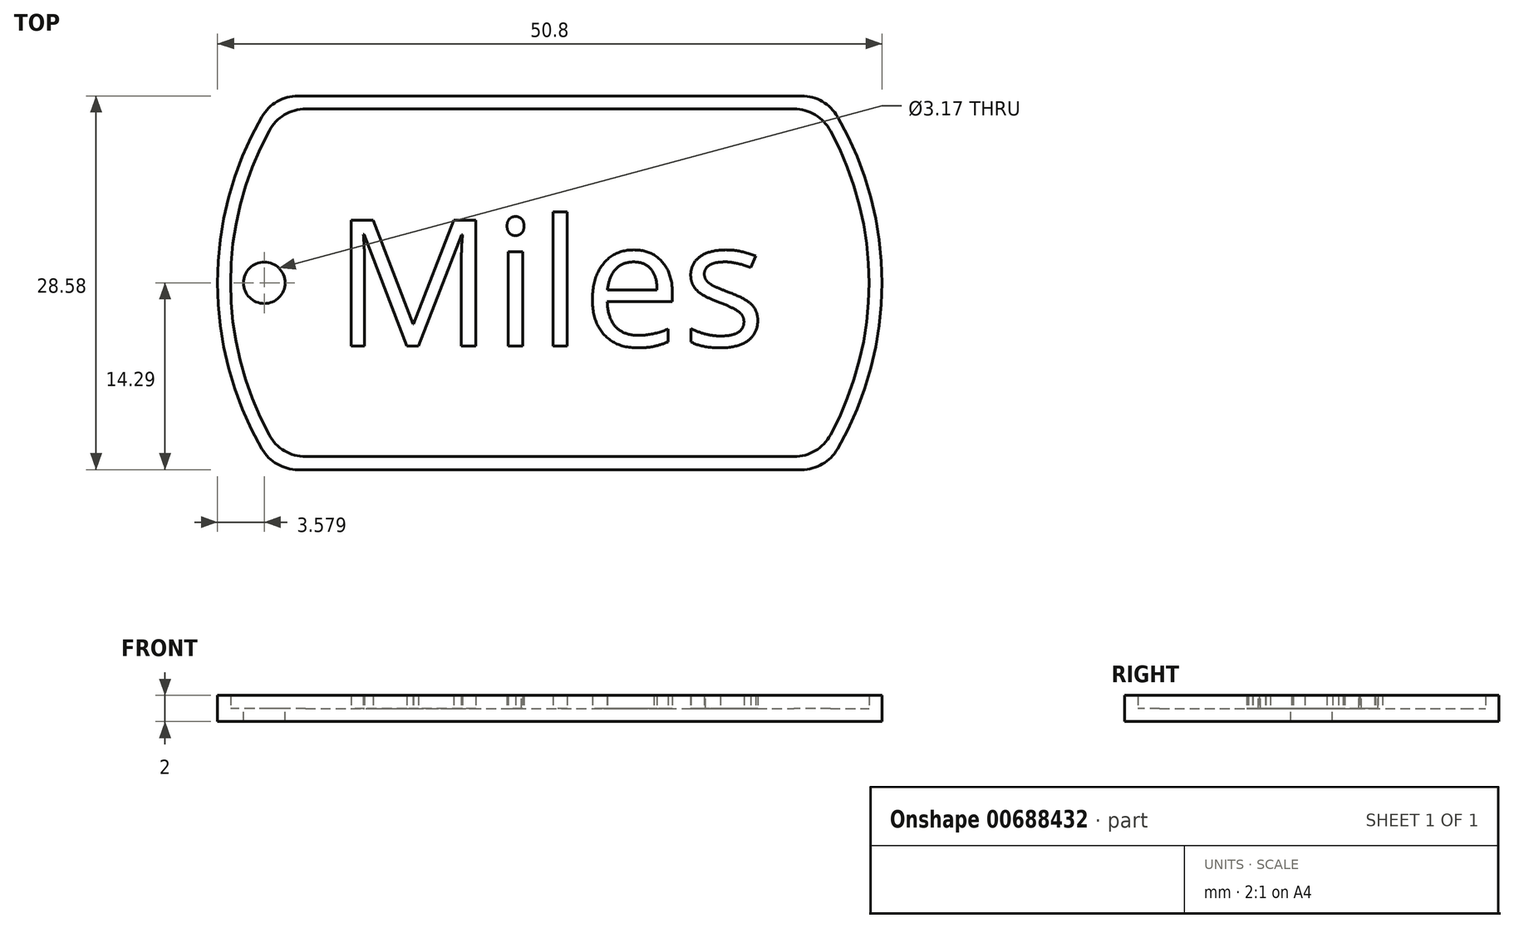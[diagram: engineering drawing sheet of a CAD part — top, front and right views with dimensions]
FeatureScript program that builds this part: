
annotation { "Feature Type Name" : "Feature", "Feature Type Description" : "" }
export const myFeature = defineFeature(function(context is Context, id is Id, definition is map)
    precondition{}
    {
        {
            var Q0;
            Q0=qCreatedBy(makeId("Top.planeOp"),FACE);
            var sketch = newSketch(context, id + "F0", { "sketchPlane" : qUnion([Q0])});
            skArc(sketch, "E0", {"start": v(-22, 12.7) * mm, "mid": v(-25.4, 0) * mm, "end": v(-22, -12.7) * mm});
            skLineSegment(sketch, "E1.top", {"start": v(-19.25, -14.29) * mm, "end": v(19.25, -14.29) * mm});
            skArc(sketch, "E2.trimOffspring", {"start": v(22, -12.7) * mm, "mid": v(25.4, 0) * mm, "end": v(22, 12.7) * mm});
            skLineSegment(sketch, "E3", {"start": v(-19.25, 14.29) * mm, "end": v(19.25, 14.29) * mm});
            skPoint(sketch, "E4.visualSharp", {"position": v(-21, 14.29) * mm});
            skArc(sketch, "E4.filletArc", {"start": v(-19.25, 14.29) * mm, "mid": v(-20.83, 13.86) * mm, "end": v(-22, 12.7) * mm});
            skPoint(sketch, "E5.visualSharp", {"position": v(21, 14.29) * mm});
            skArc(sketch, "E5.filletArc", {"start": v(22, 12.7) * mm, "mid": v(20.83, 13.86) * mm, "end": v(19.25, 14.29) * mm});
            skPoint(sketch, "E6.visualSharp", {"position": v(21, -14.29) * mm});
            skArc(sketch, "E6.filletArc", {"start": v(19.25, -14.29) * mm, "mid": v(20.83, -13.86) * mm, "end": v(22, -12.7) * mm});
            skPoint(sketch, "E7.visualSharp", {"position": v(-21, -14.29) * mm});
            skArc(sketch, "E7.filletArc", {"start": v(-22, -12.7) * mm, "mid": v(-20.83, -13.86) * mm, "end": v(-19.25, -14.29) * mm});
            skSolve(sketch);
        }
        {
            var Q0;
            Q0=makeQuery(id+"F0.imprint","IMPRINT",FACE,{"disambiguationData":[TD([[makeQuery(id+"F0.imprint","IMPRINT",EDGE,{"derivedFrom":sQuery(id+"F0.wireOp",EDGE,"E0")}),1.0]])]});
            extrude(context, id + "F1", {"entities" : qUnion([Q0]), "depth" : 1 * mm, "offsetDistance" : 25.4 * mm});
        }
        {
            var Q0;
            Q0=makeQuery(id+"F1.opExtrude","CAP_FACE",FACE,{"disambiguationData":[OSD([sQuery(id+"F0.wireOp",EDGE,"E0"),sQuery(id+"F0.wireOp",EDGE,"E1.top"),sQuery(id+"F0.wireOp",EDGE,"E2.trimOffspring"),sQuery(id+"F0.wireOp",EDGE,"E3"),sQuery(id+"F0.wireOp",EDGE,"E4.filletArc"),sQuery(id+"F0.wireOp",EDGE,"E5.filletArc"),sQuery(id+"F0.wireOp",EDGE,"E6.filletArc"),sQuery(id+"F0.wireOp",EDGE,"E7.filletArc")])],"isStart":false});
            var sketch = newSketch(context, id + "F2", { "sketchPlane" : qUnion([Q0])});
            skLineSegment(sketch, "E8.0", {"start": v(-18.66, 13.29) * mm, "end": v(18.66, 13.29) * mm});
            skArc(sketch, "E8.1", {"start": v(-21.45, 11.63) * mm, "mid": v(-24.4, 0) * mm, "end": v(-21.45, -11.63) * mm});
            skLineSegment(sketch, "E8.2", {"start": v(-18.66, -13.29) * mm, "end": v(18.66, -13.29) * mm});
            skArc(sketch, "E8.3", {"start": v(21.45, -11.63) * mm, "mid": v(24.4, 0) * mm, "end": v(21.45, 11.63) * mm});
            skPoint(sketch, "E9.visualSharp", {"position": v(-20.46, 13.29) * mm});
            skArc(sketch, "E9.filletArc", {"start": v(-18.66, 13.29) * mm, "mid": v(-20.29, 12.84) * mm, "end": v(-21.45, 11.63) * mm});
            skPoint(sketch, "E10.visualSharp", {"position": v(20.46, 13.29) * mm});
            skArc(sketch, "E10.filletArc", {"start": v(21.45, 11.63) * mm, "mid": v(20.29, 12.84) * mm, "end": v(18.66, 13.29) * mm});
            skPoint(sketch, "E11.visualSharp", {"position": v(20.46, -13.29) * mm});
            skArc(sketch, "E11.filletArc", {"start": v(18.66, -13.29) * mm, "mid": v(20.29, -12.84) * mm, "end": v(21.45, -11.63) * mm});
            skPoint(sketch, "E12.visualSharp", {"position": v(-20.46, -13.29) * mm});
            skArc(sketch, "E12.filletArc", {"start": v(-21.45, -11.63) * mm, "mid": v(-20.29, -12.84) * mm, "end": v(-18.66, -13.29) * mm});
            skLineSegment(sketch, "E13.0", {"start": v(-19.25, 14.29) * mm, "end": v(19.25, 14.29) * mm});
            skArc(sketch, "E13.1", {"start": v(-22, 12.7) * mm, "mid": v(-25.4, 0) * mm, "end": v(-22, -12.7) * mm});
            skLineSegment(sketch, "E13.2", {"start": v(-19.25, -14.29) * mm, "end": v(19.25, -14.29) * mm});
            skArc(sketch, "E13.3", {"start": v(22, -12.7) * mm, "mid": v(25.4, 0) * mm, "end": v(22, 12.7) * mm});
            skPoint(sketch, "E14.visualSharp", {"position": v(-21, -14.29) * mm});
            skArc(sketch, "E14.filletArc", {"start": v(-22, -12.7) * mm, "mid": v(-20.83, -13.86) * mm, "end": v(-19.25, -14.29) * mm});
            skPoint(sketch, "E15.visualSharp", {"position": v(21, -14.29) * mm});
            skArc(sketch, "E15.filletArc", {"start": v(19.25, -14.29) * mm, "mid": v(20.83, -13.86) * mm, "end": v(22, -12.7) * mm});
            skPoint(sketch, "E16.visualSharp", {"position": v(21, 14.29) * mm});
            skArc(sketch, "E16.filletArc", {"start": v(22, 12.7) * mm, "mid": v(20.83, 13.86) * mm, "end": v(19.25, 14.29) * mm});
            skPoint(sketch, "E17.visualSharp", {"position": v(-21, 14.29) * mm});
            skArc(sketch, "E17.filletArc", {"start": v(-19.25, 14.29) * mm, "mid": v(-20.83, 13.86) * mm, "end": v(-22, 12.7) * mm});
            skSolve(sketch);
        }
        {
            var Q0;
            Q0=makeQuery(id+"F2.imprint","IMPRINT",FACE,{"disambiguationData":[TD([[makeQuery(id+"F2.imprint","IMPRINT",EDGE,{"derivedFrom":sQuery(id+"F2.wireOp",EDGE,"E8.0")}),1.0]])]});
            extrude(context, id + "F3", {"entities" : qUnion([Q0]), "operationType" : NewBodyOperationType.ADD, "depth" : 1 * mm, "offsetDistance" : 25.4 * mm});
        }
        {
            var Q0;
            Q0=makeQuery(id+"F1.opExtrude","CAP_FACE",FACE,{"disambiguationData":[OSD([sQuery(id+"F0.wireOp",EDGE,"E0"),sQuery(id+"F0.wireOp",EDGE,"E1.top"),sQuery(id+"F0.wireOp",EDGE,"E2.trimOffspring"),sQuery(id+"F0.wireOp",EDGE,"E3"),sQuery(id+"F0.wireOp",EDGE,"E4.filletArc"),sQuery(id+"F0.wireOp",EDGE,"E5.filletArc"),sQuery(id+"F0.wireOp",EDGE,"E6.filletArc"),sQuery(id+"F0.wireOp",EDGE,"E7.filletArc")])],"isStart":false});
            var sketch = newSketch(context, id + "F4", { "sketchPlane" : qUnion([Q0])});
            skCircle(sketch, "E18", {"center": v(-21.82, 0) * mm, "radius": 1.59 * mm});
            skSolve(sketch);
        }
        {
            var Q0;
            Q0=makeQuery(id+"F4.imprint","IMPRINT",FACE,{"disambiguationData":[TD([[makeQuery(id+"F4.imprint","IMPRINT",EDGE,{"derivedFrom":sQuery(id+"F4.wireOp",EDGE,"E18")}),1.0]])]});
            extrude(context, id + "F5", {"entities" : qUnion([Q0]), "operationType" : NewBodyOperationType.REMOVE, "oppositeDirection" : true, "depth" : 1 * mm, "offsetDistance" : 25.4 * mm});
        }
        {
            var Q0;
            Q0=makeQuery(id+"F2.imprint","IMPRINT",FACE,{"disambiguationData":[TD([[makeQuery(id+"F2.imprint","IMPRINT",EDGE,{"derivedFrom":sQuery(id+"F2.wireOp",EDGE,"E8.0")}),-1.0]])]});
            var sketch = newSketch(context, id + "F6", { "sketchPlane" : qUnion([Q0])});
            skText(sketch, "E19", { "text": "Miles", "fontName": "OpenSans-Regular.ttf"});
            const initialGuessF6  = {"E19": [-0.01652, -0.00484, 1, 0, 0.00972]};
            skSetInitialGuess(sketch, initialGuessF6);
            skSolve(sketch);
        }
        {
            var Q0;
            Q0 = qSketchRegion(id + "F6", true);
            extrude(context, id + "F7", {"entities" : qUnion([Q0]), "operationType" : NewBodyOperationType.ADD, "depth" : 1 * mm, "offsetDistance" : 25.4 * mm});
        }
        {
            var Q0;
            Q0 = qConstructionFilter(qBodyType(qCreatedBy(id + "F6" ,EDGE), BodyType.WIRE), ConstructionObject.NO);
            extrude(context, id + "F8", {"bodyType" : ToolBodyType.SURFACE, "surfaceEntities" : qUnion([Q0]), "depth" : 1 * mm, "offsetDistance" : 25.4 * mm});
        }
    });
